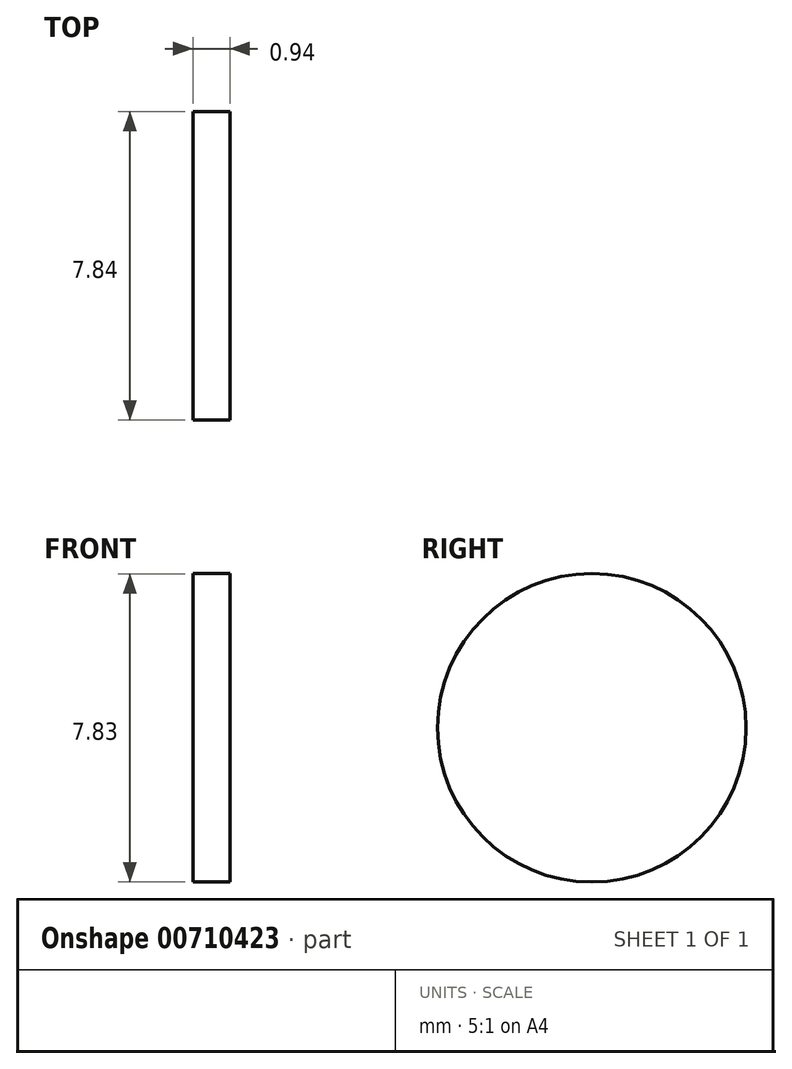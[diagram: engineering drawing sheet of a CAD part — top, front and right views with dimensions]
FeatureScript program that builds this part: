
annotation { "Feature Type Name" : "Feature", "Feature Type Description" : "" }
export const myFeature = defineFeature(function(context is Context, id is Id, definition is map)
    precondition{}
    {
        {
            var Q0;
            Q0=qCreatedBy(makeId("Right.planeOp"),FACE);
            var sketch = newSketch(context, id + "F0", { "sketchPlane" : qUnion([Q0])});
            skCircle(sketch, "E0", {"center": v(0, 31.83) * mm, "radius": 3.92 * mm});
            skFitSpline(sketch, "E1", {"points": [v(0, 35.75) * mm, v(14.6, 31.83) * mm, v(41.43, 35.74) * mm, v(75.7, 31.83) * mm, v(74.34, 31.83) * mm, v(74.39, 31.83) * mm], "startDerivative": vector(60.14, -24.84) * mm, "endDerivative": vector(6.26, -0.15) * mm});
            skSolve(sketch);
        }
        {
            var Q0;
            {var subQ0=sQuery(id+"F0.wireOp",EDGE,"E1");var subQ1=sQuery(id+"F0.wireOp",EDGE,"E0");var subQ2=makeQuery(id+"F0.imprint","INTERSECT",VERTEX,{"disambiguationData":[OD(0.0)],"derivedFrom":[subQ1,subQ0]});Q0=makeQuery(id+"F0.imprint","IMPRINT",FACE,{"disambiguationData":[TD([[makeQuery(id+"F0.imprint","IMPRINT",EDGE,{"disambiguationData":[TD([[subQ2,-1.0]])],"derivedFrom":subQ1}),1.0]])]});}
            var Q1;
            {var subQ0=sQuery(id+"F0.wireOp",EDGE,"E1");var subQ1=sQuery(id+"F0.wireOp",EDGE,"E0");var subQ2=makeQuery(id+"F0.imprint","INTERSECT",VERTEX,{"disambiguationData":[OD(0.0)],"derivedFrom":[subQ1,subQ0]});Q1=makeQuery(id+"F0.imprint","IMPRINT",FACE,{"disambiguationData":[TD([[makeQuery(id+"F0.imprint","IMPRINT",EDGE,{"disambiguationData":[TD([[subQ2,1.0]])],"derivedFrom":subQ1}),1.0]])]});}
            extrude(context, id + "F1", {"entities" : qUnion([Q0, Q1]), "depth" : 0.94 * mm, "offsetDistance" : 25.4 * mm});
        }
    });
